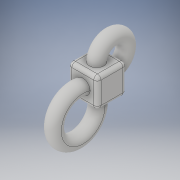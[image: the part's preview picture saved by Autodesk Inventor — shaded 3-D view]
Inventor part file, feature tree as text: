
AUTODESK INVENTOR PART (.ipt)
format: ipt  version: 2017 (Build 210142000, 142)  size: 346,112 bytes
history: native  units: in
note: dims shown in document units (in); Inventor stores cm internally (conversion verified against a paired STEP export)
features: sketch x7, fillet x5, sweep x2, extrude x1, plane x1
ambient origin geometry x8: Origin, YZ Plane, XZ Plane, XY Plane, X Axis, Y Axis, Z Axis, Center Point
bodies: Solid1 (feature_tree)
feature tree (16):
  extrude  "Extrusion1"  Depth=1.0in
  sketch  "Sketch2"  dims[d2=1.0in d3=0.0in d4=0.5in]
  sketch  "Sketch3"  dims[d5=0.5in d6=0.5in d7=0.5in d8=0.5in d9=0.5in d10=0.5in d11=0.5in]
  sketch  "Sketch4"  dims[d12=0.5in]
  sketch  "Sketch5"  dims[d13=0.5in]
  plane  "Work Plane1"
  sweep  "Sweep1"
  sweep  "Sweep2"
  fillet  "Fillet1"  Radius=0.5in
  fillet  "Fillet2"  Radius=0.5in
  fillet  "Fillet3"  Radius=0.5in
  fillet  "Fillet4"  Radius=0.5in
  fillet  "Fillet5"  Radius=0.5in
  sketch  "Sketch1"  dims[d0=1.0in d1=1.0in]
  sketch  "Sketch6"  dims[d14=0.5in]
  sketch  "Sketch7"  dims[d15=0.5in d17=0.75in d18=0.5in d19=0.75in d21=0.0in d22=0.0in d23=0.5in d24=0.0in d25=0.0in d26=0.125in d27=0.125in d28=0.125in d29=0.125in d30=0.125in]
